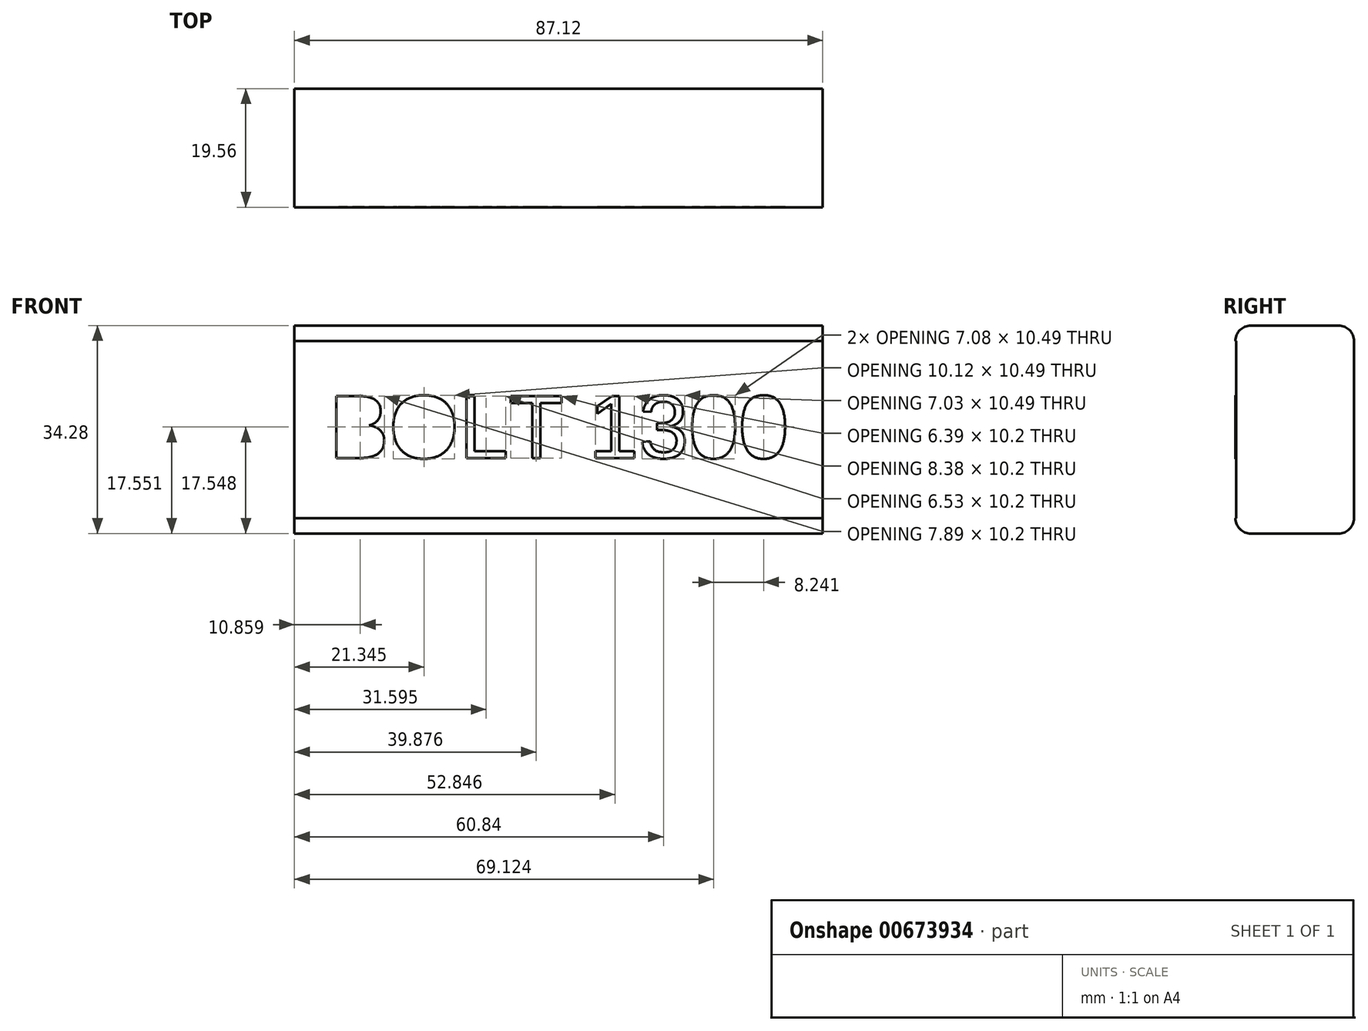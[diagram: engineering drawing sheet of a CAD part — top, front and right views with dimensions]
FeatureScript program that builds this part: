
annotation { "Feature Type Name" : "Feature", "Feature Type Description" : "" }
export const myFeature = defineFeature(function(context is Context, id is Id, definition is map)
    precondition{}
    {
        {
            var Q0;
            Q0=qCreatedBy(makeId("Front.planeOp"),FACE);
            var sketch = newSketch(context, id + "F0", { "sketchPlane" : qUnion([Q0])});
            skLineSegment(sketch, "E0.bottom", {"start": v(-43.56, 17.15) * mm, "end": v(43.56, 17.15) * mm});
            skLineSegment(sketch, "E0.top", {"start": v(-43.56, -17.14) * mm, "end": v(43.56, -17.14) * mm});
            skLineSegment(sketch, "E0.left", {"start": v(-43.56, 17.15) * mm, "end": v(-43.56, -17.15) * mm});
            skLineSegment(sketch, "E0.right", {"start": v(43.56, 17.15) * mm, "end": v(43.56, -17.14) * mm});
            skPoint(sketch, "E0.middle", {"position": v(0, 0) * mm});
            skSolve(sketch);
        }
        {
            var Q0;
            Q0 = qSketchRegion(id + "F0", true);
            extrude(context, id + "F1", {"entities" : qUnion([Q0]), "endBound" : BoundingType.SYMMETRIC, "depth" : 19.56 * mm, "offsetDistance" : 25.4 * mm});
        }
        {
            var Q0;
            Q0=makeQuery(id+"F1.opExtrude","CAP_EDGE",EDGE,{"disambiguationData":[OSD([sQuery(id+"F0.wireOp",EDGE,"E0.bottom")])],"isStart":true});
            var Q1;
            Q1=makeQuery(id+"F1.opExtrude","CAP_EDGE",EDGE,{"disambiguationData":[OSD([sQuery(id+"F0.wireOp",EDGE,"E0.top")])],"isStart":true});
            var Q2;
            Q2=makeQuery(id+"F1.opExtrude","CAP_EDGE",EDGE,{"disambiguationData":[OSD([sQuery(id+"F0.wireOp",EDGE,"E0.bottom")])],"isStart":false});
            var Q3;
            Q3=makeQuery(id+"F1.opExtrude","CAP_EDGE",EDGE,{"disambiguationData":[OSD([sQuery(id+"F0.wireOp",EDGE,"E0.top")])],"isStart":false});
            fillet(context, id + "F2", {"entities" : qUnion([Q0, Q1, Q2, Q3]), "radius" : 2.54 * mm, "tangentPropagation" : true, "allowEdgeOverflow" : false});
        }
        {
            var Q0;
            Q0=makeQuery(id+"F1.opExtrude","CAP_FACE",FACE,{"disambiguationData":[OSD([sQuery(id+"F0.wireOp",EDGE,"E0.bottom"),sQuery(id+"F0.wireOp",EDGE,"E0.top"),sQuery(id+"F0.wireOp",EDGE,"E0.left"),sQuery(id+"F0.wireOp",EDGE,"E0.right")])],"isStart":false});
            var sketch = newSketch(context, id + "F3", { "sketchPlane" : qUnion([Q0])});
            skText(sketch, "E1", { "text": "BOLT 1300", "fontName": "Arimo-Regular.ttf"});
            const initialGuessF3  = {"E1": [-0.03786, -0.00469, 1, 0, 0.01067]};
            skSetInitialGuess(sketch, initialGuessF3);
            skSolve(sketch);
        }
        {
            var Q0;
            Q0=makeQuery(id+"F3.imprint","IMPRINT",FACE,{"disambiguationData":[TD([[makeQuery(id+"F3.imprint","IMPRINT",EDGE,{"derivedFrom":sQuery(id+"F3.wireOp",EDGE,"E1.sketch_text.stroke-0")}),1.0]])]});
            extrude(context, id + "F4", {"entities" : qUnion([Q0]), "operationType" : NewBodyOperationType.REMOVE, "oppositeDirection" : true, "depth" : 0.13 * mm, "offsetDistance" : 25.4 * mm});
        }
        {
            var Q0;
            Q0=makeQuery(id+"F1.opExtrude","SWEPT_BODY",BODY,{"disambiguationData":[OSD([sQuery(id+"F0.wireOp",EDGE,"E0.bottom"),sQuery(id+"F0.wireOp",EDGE,"E0.top"),sQuery(id+"F0.wireOp",EDGE,"E0.left"),sQuery(id+"F0.wireOp",EDGE,"E0.right")])]});
            transform(context, id + "F5", {"entities" : qUnion([Q0]), "transformType" : TransformType.TRANSLATION_3D, "dx" : 0 * mm, "dy" : 0 * mm, "dz" : 0 * mm, "makeCopy" : true});
        }
    });
